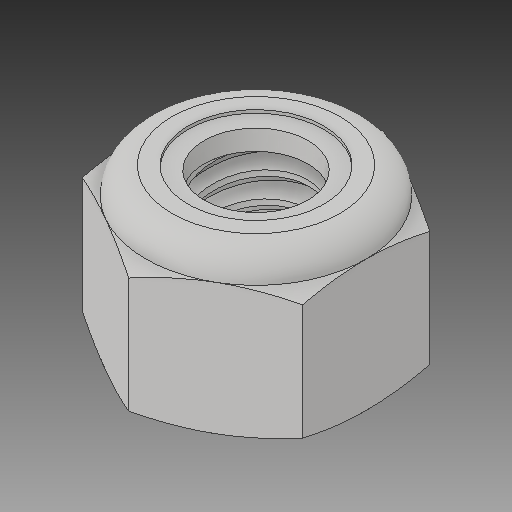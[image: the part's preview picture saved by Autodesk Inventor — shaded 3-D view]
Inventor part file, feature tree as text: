
AUTODESK INVENTOR PART (.ipt)
format: ipt  version: 2017 SP1 (Build 210196100, 196)  size: 314,368 bytes
history: native  units: in
note: dims shown in document units (in); Inventor stores cm internally (conversion verified against a paired STEP export)
features: other x1, revolve x1
ambient origin geometry x8: Origin, YZ Plane, XZ Plane, XY Plane, X Axis, Y Axis, Z Axis, Center Point
bodies: Solid1 (feature_tree), Solid2 (feature_tree)
feature tree (2):
  other  "Cut-Revolve4"
  revolve  "Revolve2"  [1 undecoded]
note: 1 required parameter value undecoded (feature->parameter linkage not recoverable at this tier; creation-order binding heuristic only, values carry confidence <= 0.55)
